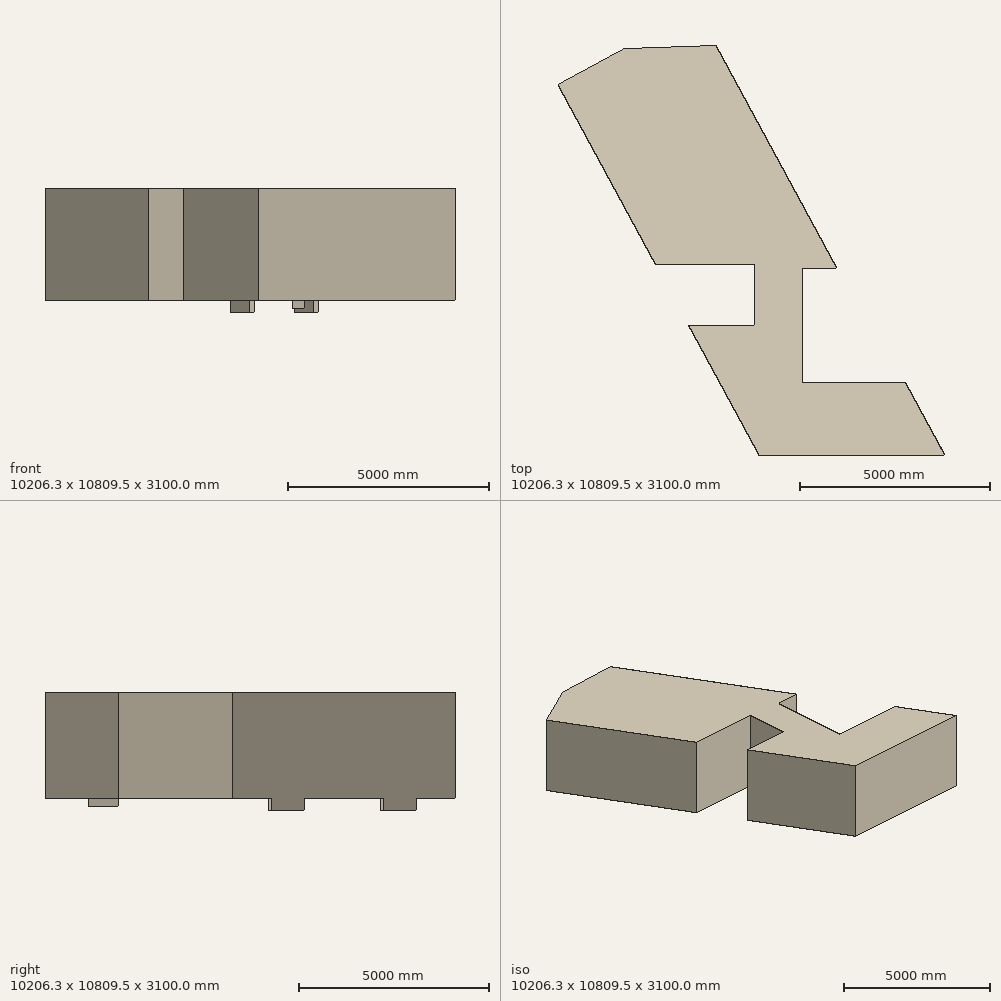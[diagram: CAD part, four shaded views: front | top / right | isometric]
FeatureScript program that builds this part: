
annotation { "Feature Type Name" : "Feature", "Feature Type Description" : "" }
export const myFeature = defineFeature(function(context is Context, id is Id, definition is map)
    precondition{}
    {
        {
            var Q0;
            Q0=qCreatedBy(makeId("Top.planeOp"),FACE);
            var sketch = newSketch(context, id + "F0", { "sketchPlane" : qUnion([Q0])});
            skLineSegment(sketch, "E0", {"start": v(0, 0) * mm, "end": v(-1860.92, 3427.39) * mm});
            skLineSegment(sketch, "E1", {"start": v(0, 0) * mm, "end": v(-8944.13, 0) * mm, "construction": true});
            skLineSegment(sketch, "E2", {"start": v(0, 0) * mm, "end": v(4900, 0) * mm});
            skLineSegment(sketch, "E3", {"start": v(4900, 0) * mm, "end": v(3850.25, 1933.4) * mm});
            skLineSegment(sketch, "E4", {"start": v(3850.25, 1933.4) * mm, "end": v(1150.25, 1933.4) * mm});
            skLineSegment(sketch, "E5", {"start": v(1150.25, 1933.4) * mm, "end": v(1150.25, 4933.4) * mm});
            skLineSegment(sketch, "E6", {"start": v(1150.25, 4933.4) * mm, "end": v(2050.25, 4933.4) * mm});
            skLineSegment(sketch, "E7", {"start": v(2050.25, 4933.4) * mm, "end": v(-3013.22, 14259.15) * mm, "construction": true});
            skPoint(sketch, "E8", {"position": v(-1140.19, 10809.45) * mm});
            skLineSegment(sketch, "E9", {"start": v(-1140.19, 10809.45) * mm, "end": v(2050.25, 4933.4) * mm});
            skLineSegment(sketch, "E10", {"start": v(-1860.92, 3427.39) * mm, "end": v(-110.92, 3427.39) * mm});
            skLineSegment(sketch, "E11", {"start": v(-110.92, 3427.39) * mm, "end": v(-110.92, 5027.39) * mm});
            skLineSegment(sketch, "E12", {"start": v(0, 0) * mm, "end": v(-7639.98, 14071.09) * mm, "construction": true});
            skLineSegment(sketch, "E13", {"start": v(-110.92, 5027.39) * mm, "end": v(-2729.65, 5027.39) * mm});
            skLineSegment(sketch, "E14", {"start": v(-2729.65, 5027.39) * mm, "end": v(-5306.3, 9773) * mm});
            skLineSegment(sketch, "E15", {"start": v(-5306.3, 9773) * mm, "end": v(-3548.67, 10727.32) * mm});
            skLineSegment(sketch, "E16", {"start": v(-3548.67, 10727.32) * mm, "end": v(-1140.19, 10809.45) * mm});
            skSolve(sketch);
        }
        {
            var Q0;
            Q0=makeQuery(id+"F0.imprint","IMPRINT",FACE,{"disambiguationData":[TD([[makeQuery(id+"F0.imprint","IMPRINT",EDGE,{"derivedFrom":sQuery(id+"F0.wireOp",EDGE,"E0")}),-1.0]])]});
            extrude(context, id + "F1", {"entities" : qUnion([Q0]), "depth" : 2800 * mm});
        }
        {
            var Q0;
            Q0=makeQuery(id+"F1.opExtrude","CAP_FACE",FACE,{"disambiguationData":[OSD([sQuery(id+"F0.wireOp",EDGE,"E0"),sQuery(id+"F0.wireOp",EDGE,"E2"),sQuery(id+"F0.wireOp",EDGE,"E3"),sQuery(id+"F0.wireOp",EDGE,"E4"),sQuery(id+"F0.wireOp",EDGE,"E5"),sQuery(id+"F0.wireOp",EDGE,"E6"),sQuery(id+"F0.wireOp",EDGE,"E9"),sQuery(id+"F0.wireOp",EDGE,"E10"),sQuery(id+"F0.wireOp",EDGE,"E11"),sQuery(id+"F0.wireOp",EDGE,"E13"),sQuery(id+"F0.wireOp",EDGE,"E14"),sQuery(id+"F0.wireOp",EDGE,"E15"),sQuery(id+"F0.wireOp",EDGE,"E16")])],"isStart":true});
            var sketch = newSketch(context, id + "F2", { "sketchPlane" : qUnion([Q0])});
            skLineSegment(sketch, "E17", {"start": v(455.03, -7871.42) * mm, "end": v(-994.32, -7084.5) * mm, "construction": true});
            skLineSegment(sketch, "E18.0", {"start": v(-1140.19, -10809.45) * mm, "end": v(2050.25, -4933.4) * mm});
            skLineSegment(sketch, "E19", {"start": v(2050.25, -4933.4) * mm, "end": v(1253.4, -6401.02) * mm, "construction": true});
            skLineSegment(sketch, "E20", {"start": v(455.03, -7871.42) * mm, "end": v(-341.82, -9339.05) * mm, "construction": true});
            skLineSegment(sketch, "E21", {"start": v(1253.4, -6401.02) * mm, "end": v(1014.82, -6840.43) * mm});
            skLineSegment(sketch, "E22", {"start": v(1014.82, -6840.43) * mm, "end": v(883, -6768.86) * mm});
            skLineSegment(sketch, "E23", {"start": v(883, -6768.86) * mm, "end": v(1360.15, -5890.04) * mm});
            skLineSegment(sketch, "E24", {"start": v(1360.15, -5890.04) * mm, "end": v(1491.97, -5961.61) * mm});
            skLineSegment(sketch, "E25", {"start": v(1491.97, -5961.61) * mm, "end": v(1014.82, -6840.43) * mm});
            skLineSegment(sketch, "E26", {"start": v(-341.82, -9339.05) * mm, "end": v(-580.4, -9778.46) * mm});
            skLineSegment(sketch, "E27", {"start": v(-580.4, -9778.46) * mm, "end": v(-712.22, -9706.88) * mm});
            skLineSegment(sketch, "E28", {"start": v(-712.22, -9706.88) * mm, "end": v(-235.07, -8828.07) * mm});
            skLineSegment(sketch, "E29", {"start": v(-235.07, -8828.07) * mm, "end": v(-103.24, -8899.64) * mm});
            skLineSegment(sketch, "E30", {"start": v(-103.24, -8899.64) * mm, "end": v(-580.4, -9778.46) * mm});
            skLineSegment(sketch, "E31.bottom", {"start": v(1150.25, -1933.4) * mm, "end": v(850.25, -1933.4) * mm});
            skLineSegment(sketch, "E31.top", {"start": v(1150.25, -1133.4) * mm, "end": v(850.25, -1133.4) * mm});
            skLineSegment(sketch, "E31.left", {"start": v(1150.25, -1933.4) * mm, "end": v(1150.25, -1133.4) * mm});
            skLineSegment(sketch, "E31.right", {"start": v(850.25, -1933.4) * mm, "end": v(850.25, -1133.4) * mm});
            skSolve(sketch);
        }
        {
            var Q0;
            Q0=makeQuery(id+"F2.imprint","IMPRINT",FACE,{"disambiguationData":[TD([[makeQuery(id+"F2.imprint","IMPRINT",EDGE,{"derivedFrom":sQuery(id+"F2.wireOp",EDGE,"E31.bottom")}),-1.0]])]});
            extrude(context, id + "F3", {"entities" : qUnion([Q0]), "operationType" : NewBodyOperationType.ADD, "depth" : 200 * mm});
        }
        {
            var Q0;
            {var subQ0=sQuery(id+"F2.wireOp",EDGE,"E22");Q0=makeQuery(id+"F2.imprint","IMPRINT",FACE,{"disambiguationData":[TD([[makeQuery(id+"F2.imprint","IMPRINT",EDGE,{"derivedFrom":subQ0}),-1.0]])]});}
            var Q1;
            {var subQ0=sQuery(id+"F2.wireOp",EDGE,"E27");Q1=makeQuery(id+"F2.imprint","IMPRINT",FACE,{"disambiguationData":[TD([[makeQuery(id+"F2.imprint","IMPRINT",EDGE,{"derivedFrom":subQ0}),-1.0]])]});}
            extrude(context, id + "F4", {"entities" : qUnion([Q0, Q1]), "operationType" : NewBodyOperationType.ADD, "depth" : 300 * mm});
        }
    });
